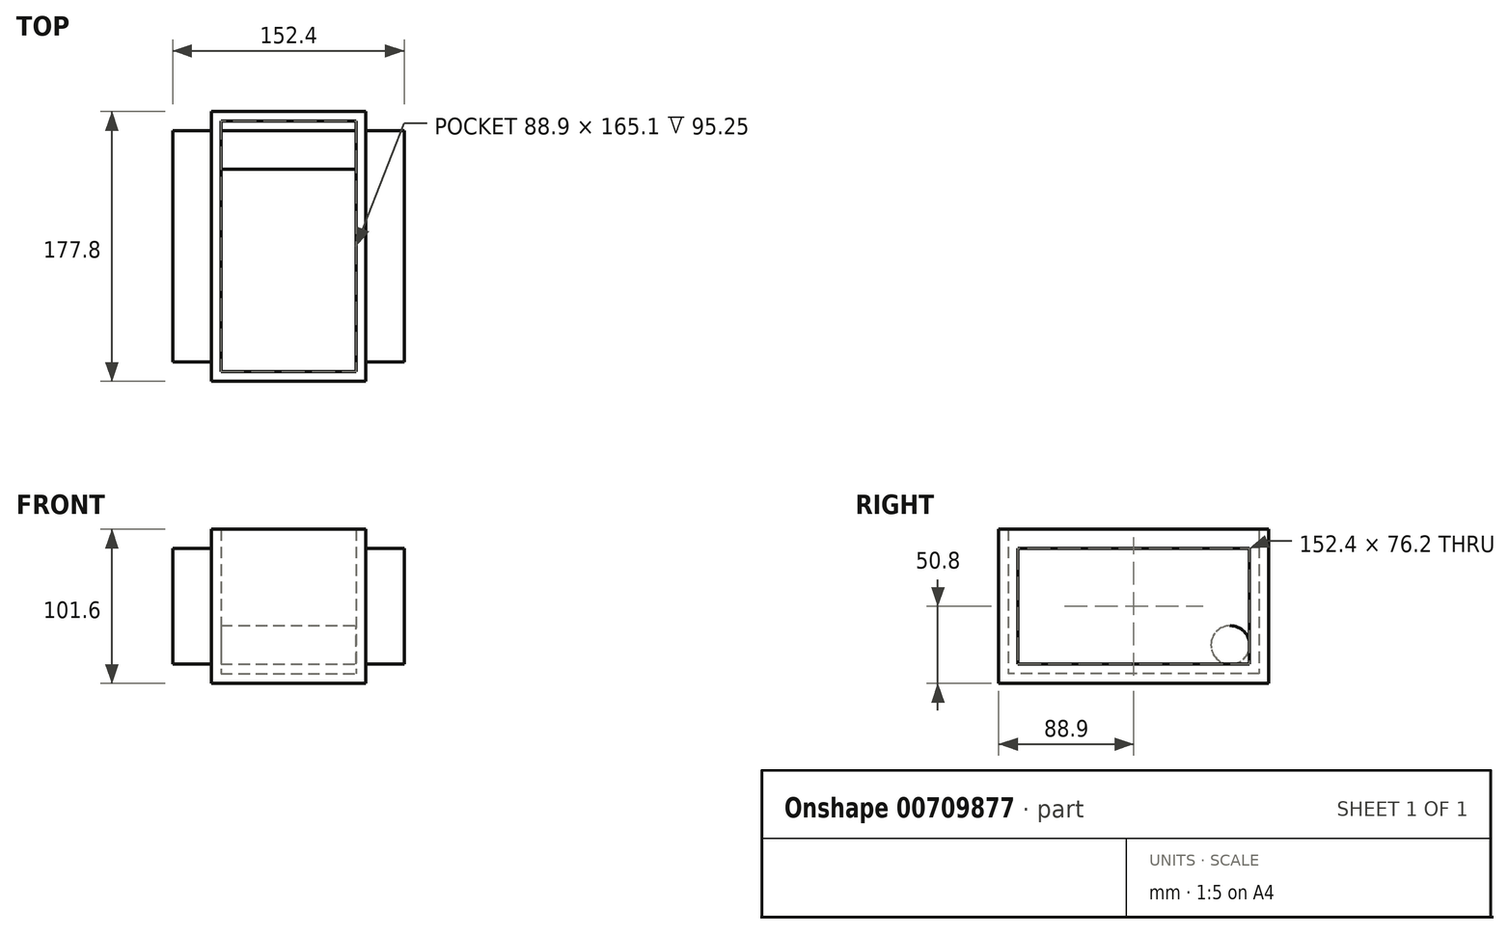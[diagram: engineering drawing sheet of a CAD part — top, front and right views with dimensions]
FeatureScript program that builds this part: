
annotation { "Feature Type Name" : "Feature", "Feature Type Description" : "" }
export const myFeature = defineFeature(function(context is Context, id is Id, definition is map)
    precondition{}
    {
        {
            var Q0;
            Q0=qCreatedBy(makeId("Top.planeOp"),FACE);
            var sketch = newSketch(context, id + "F0", { "sketchPlane" : qUnion([Q0])});
            skLineSegment(sketch, "E0.bottom", {"start": v(-50.8, 88.9) * mm, "end": v(50.8, 88.9) * mm});
            skLineSegment(sketch, "E0.top", {"start": v(-50.8, -88.9) * mm, "end": v(50.8, -88.9) * mm});
            skLineSegment(sketch, "E0.left", {"start": v(-50.8, 88.9) * mm, "end": v(-50.8, -88.9) * mm});
            skLineSegment(sketch, "E0.right", {"start": v(50.8, 88.9) * mm, "end": v(50.8, -88.9) * mm});
            skSolve(sketch);
        }
        {
            var Q0;
            Q0=makeQuery(id+"F0.imprint","IMPRINT",FACE,{"disambiguationData":[TD([[makeQuery(id+"F0.imprint","IMPRINT",EDGE,{"derivedFrom":sQuery(id+"F0.wireOp",EDGE,"E0.bottom")}),-1.0]])]});
            extrude(context, id + "F1", {"entities" : qUnion([Q0]), "endBound" : BoundingType.SYMMETRIC, "depth" : 101.6 * mm, "offsetDistance" : 25.4 * mm});
        }
        {
            var Q0;
            Q0=makeQuery(id+"F1.opExtrude","CAP_FACE",FACE,{"disambiguationData":[OSD([sQuery(id+"F0.wireOp",EDGE,"E0.bottom"),sQuery(id+"F0.wireOp",EDGE,"E0.top"),sQuery(id+"F0.wireOp",EDGE,"E0.left"),sQuery(id+"F0.wireOp",EDGE,"E0.right")])],"isStart":false});
            shell(context, id + "F2", {"entities" : qUnion([Q0]), "thickness" : 6.35 * mm});
        }
        {
            var Q0;
            Q0=makeQuery(id+"F1.opExtrude","SWEPT_FACE",FACE,{"disambiguationData":[OSD([sQuery(id+"F0.wireOp",EDGE,"E0.left")])]});
            var sketch = newSketch(context, id + "F3", { "sketchPlane" : qUnion([Q0])});
            skLineSegment(sketch, "E1.bottom", {"start": v(-76.2, 38.1) * mm, "end": v(76.2, 38.1) * mm});
            skLineSegment(sketch, "E1.top", {"start": v(-76.2, -38.1) * mm, "end": v(76.2, -38.1) * mm});
            skLineSegment(sketch, "E1.left", {"start": v(-76.2, 38.1) * mm, "end": v(-76.2, -38.1) * mm});
            skLineSegment(sketch, "E1.right", {"start": v(76.2, 38.1) * mm, "end": v(76.2, -38.1) * mm});
            skSolve(sketch);
        }
        {
            var Q0;
            Q0=qSketchRegion(id+"F3",true);
            extrude(context, id + "F4", {"entities" : qUnion([Q0]), "operationType" : NewBodyOperationType.ADD, "depth" : 25.4 * mm, "offsetDistance" : 25.4 * mm});
        }
        {
            var Q0;
            Q0=makeQuery(id+"F1.opExtrude","SWEPT_FACE",FACE,{"disambiguationData":[OSD([sQuery(id+"F0.wireOp",EDGE,"E0.right")])]});
            var sketch = newSketch(context, id + "F5", { "sketchPlane" : qUnion([Q0])});
            skLineSegment(sketch, "E2.bottom", {"start": v(-76.2, 38.1) * mm, "end": v(76.2, 38.1) * mm});
            skLineSegment(sketch, "E2.top", {"start": v(-76.2, -38.1) * mm, "end": v(76.2, -38.1) * mm});
            skLineSegment(sketch, "E2.left", {"start": v(-76.2, 38.1) * mm, "end": v(-76.2, -38.1) * mm});
            skLineSegment(sketch, "E2.right", {"start": v(76.2, 38.1) * mm, "end": v(76.2, -38.1) * mm});
            skSolve(sketch);
        }
        {
            var Q0;
            Q0=qSketchRegion(id+"F5",true);
            extrude(context, id + "F6", {"entities" : qUnion([Q0]), "operationType" : NewBodyOperationType.ADD, "depth" : 25.4 * mm, "offsetDistance" : 25.4 * mm});
        }
        {
            var Q0;
            Q0=makeQuery(id+"F2.opShell","OFFSET_FACE",FACE,{"disambiguationData":[OSD([sQuery(id+"F0.wireOp",EDGE,"E0.right")])]});
            var sketch = newSketch(context, id + "F7", { "sketchPlane" : qUnion([Q0])});
            skCircle(sketch, "E3", {"center": v(-63.5, -25.4) * mm, "radius": 12.7 * mm});
            skSolve(sketch);
        }
        {
            var Q0;
            Q0=makeQuery(id+"F7.imprint","IMPRINT",FACE,{"disambiguationData":[TD([[makeQuery(id+"F7.imprint","IMPRINT",EDGE,{"derivedFrom":sQuery(id+"F7.wireOp",EDGE,"E3")}),1.0]])]});
            extrude(context, id + "F8", {"entities" : qUnion([Q0]), "operationType" : NewBodyOperationType.ADD, "depth" : 88.9 * mm, "offsetDistance" : 25.4 * mm});
        }
    });
